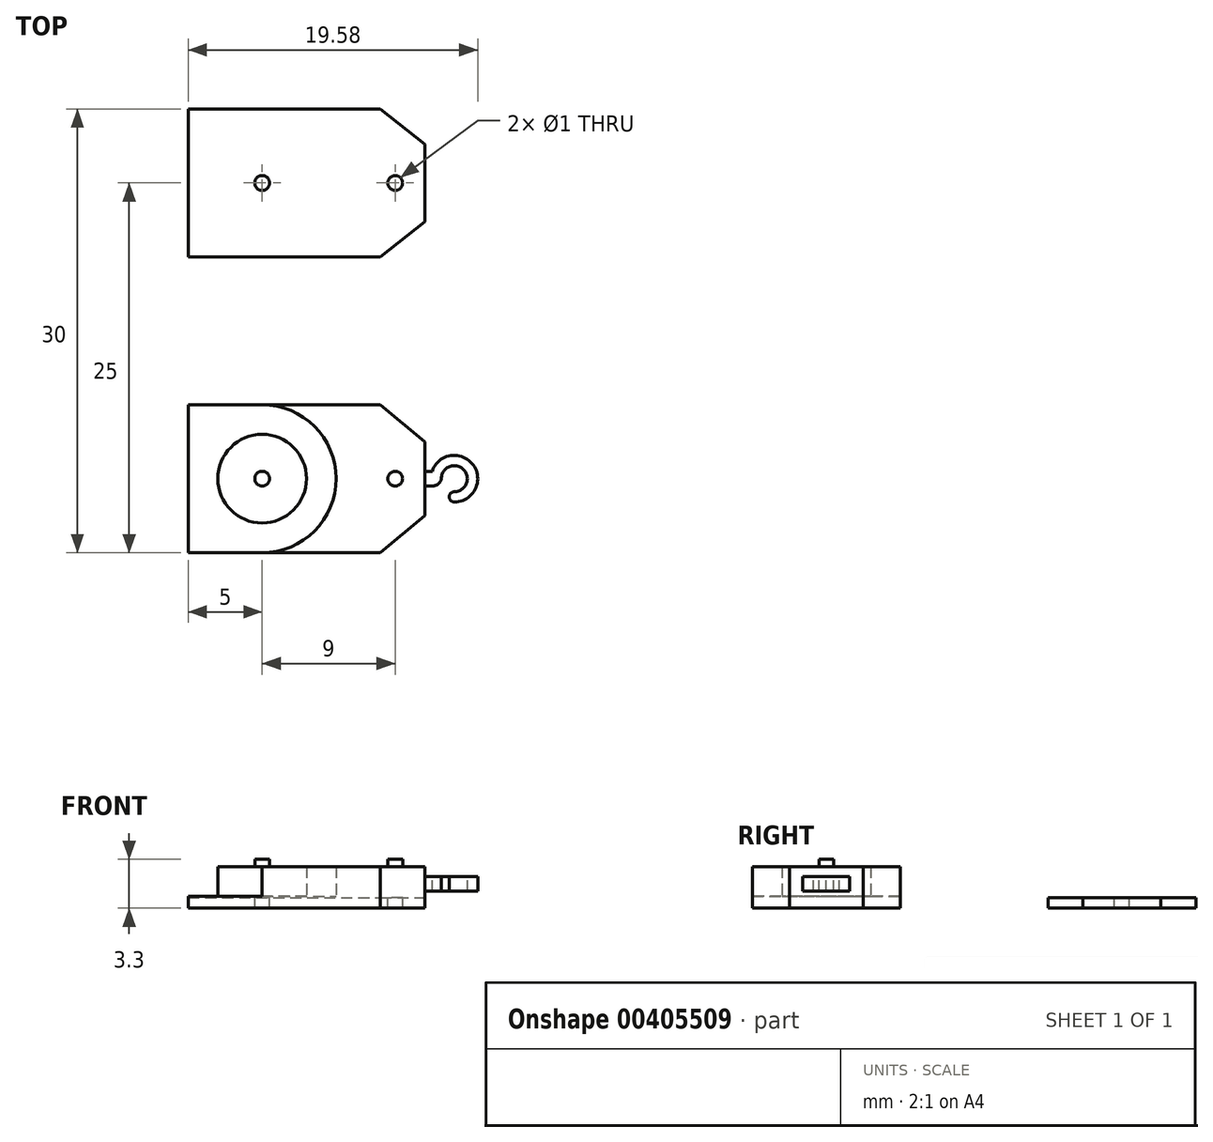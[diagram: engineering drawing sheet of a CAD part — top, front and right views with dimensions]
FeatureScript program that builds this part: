
annotation { "Feature Type Name" : "Feature", "Feature Type Description" : "" }
export const myFeature = defineFeature(function(context is Context, id is Id, definition is map)
    precondition{}
    {
        {
            var Q0;
            Q0=qCreatedBy(makeId("Top.planeOp"),FACE);
            var sketch = newSketch(context, id + "F0", { "sketchPlane" : qUnion([Q0])});
            skLineSegment(sketch, "E0", {"start": v(0, 0) * mm, "end": v(0, -10) * mm});
            skLineSegment(sketch, "E1", {"start": v(0, -10) * mm, "end": v(13, -10) * mm});
            skLineSegment(sketch, "E2", {"start": v(0, 0) * mm, "end": v(13, 0) * mm});
            skLineSegment(sketch, "E3", {"start": v(13, 0) * mm, "end": v(16, -2.5) * mm});
            skLineSegment(sketch, "E4", {"start": v(16, -2.5) * mm, "end": v(16, -7.5) * mm});
            skLineSegment(sketch, "E5", {"start": v(16, -7.5) * mm, "end": v(13, -10) * mm});
            skLineSegment(sketch, "E6", {"start": v(16, -5) * mm, "end": v(0, -5) * mm, "construction": true});
            skSolve(sketch);
        }
        {
            var Q0;
            Q0=makeQuery(id+"F0.imprint","IMPRINT",FACE,{"disambiguationData":[TD([[makeQuery(id+"F0.imprint","IMPRINT",EDGE,{"derivedFrom":sQuery(id+"F0.wireOp",EDGE,"E0")}),1.0]])]});
            extrude(context, id + "F1", {"entities" : qUnion([Q0]), "depth" : 0.8 * mm});
        }
        {
            var Q0;
            Q0=makeQuery(id+"F1.opExtrude","CAP_FACE",FACE,{"disambiguationData":[OSD([sQuery(id+"F0.wireOp",EDGE,"E0"),sQuery(id+"F0.wireOp",EDGE,"E1"),sQuery(id+"F0.wireOp",EDGE,"E2"),sQuery(id+"F0.wireOp",EDGE,"E3"),sQuery(id+"F0.wireOp",EDGE,"E4"),sQuery(id+"F0.wireOp",EDGE,"E5")])],"isStart":false});
            var sketch = newSketch(context, id + "F2", { "sketchPlane" : qUnion([Q0])});
            skLineSegment(sketch, "E7", {"start": v(0, -5) * mm, "end": v(5, -5) * mm, "construction": true});
            skCircle(sketch, "E8", {"center": v(5, -5) * mm, "radius": 3 * mm});
            skLineSegment(sketch, "E9", {"start": v(0, 0) * mm, "end": v(0, -1) * mm, "construction": true});
            skArc(sketch, "E10", {"start": v(5, 0) * mm, "mid": v(10, -5) * mm, "end": v(5, -10) * mm});
            skArc(sketch, "E11", {"start": v(5, -1) * mm, "mid": v(9, -5) * mm, "end": v(5, -9) * mm});
            skLineSegment(sketch, "E12", {"start": v(0, -1) * mm, "end": v(5, -1) * mm});
            skLineSegment(sketch, "E13", {"start": v(5, -9) * mm, "end": v(0, -9) * mm});
            skLineSegment(sketch, "E14", {"start": v(0, -9) * mm, "end": v(0, -10) * mm});
            skLineSegment(sketch, "E15", {"start": v(0, -10) * mm, "end": v(5, -10) * mm});
            skLineSegment(sketch, "E16", {"start": v(0, 0) * mm, "end": v(5, 0) * mm});
            skLineSegment(sketch, "E17", {"start": v(16, -7.5) * mm, "end": v(13, -10) * mm});
            skLineSegment(sketch, "E18", {"start": v(13, -10) * mm, "end": v(12, -10) * mm});
            skLineSegment(sketch, "E19", {"start": v(12, -10) * mm, "end": v(12, 0) * mm});
            skLineSegment(sketch, "E20", {"start": v(12, 0) * mm, "end": v(13, 0) * mm});
            skLineSegment(sketch, "E21", {"start": v(13, 0) * mm, "end": v(16, -2.5) * mm});
            skLineSegment(sketch, "E22", {"start": v(16, -2.5) * mm, "end": v(16, -7.5) * mm});
            skSolve(sketch);
        }
        {
            var Q0;
            Q0 = qSketchRegion(id + "F2", true);
            var Q1;
            Q1=makeQuery(id+"F2.imprint","IMPRINT",FACE,{"disambiguationData":[TD([[makeQuery(id+"F2.imprint","IMPRINT",EDGE,{"derivedFrom":sQuery(id+"F2.wireOp",EDGE,"E10")}),-1.0]])]});
            extrude(context, id + "F3", {"entities" : qUnion([Q0, Q1]), "operationType" : NewBodyOperationType.ADD, "depth" : 2 * mm});
        }
        {
            var Q0;
            Q0=makeQuery(id+"F3.opExtrude","CAP_FACE",FACE,{"disambiguationData":[OSD([sQuery(id+"F2.wireOp",EDGE,"E8")])],"isStart":false});
            var sketch = newSketch(context, id + "F4", { "sketchPlane" : qUnion([Q0])});
            skCircle(sketch, "E23", {"center": v(5, -5) * mm, "radius": 0.5 * mm});
            skSolve(sketch);
        }
        {
            var Q0;
            Q0 = qSketchRegion(id + "F4", true);
            extrude(context, id + "F5", {"entities" : qUnion([Q0]), "operationType" : NewBodyOperationType.ADD, "depth" : 0.5 * mm});
        }
        {
            var Q0;
            Q0=makeQuery(id+"F3.opExtrude","CAP_FACE",FACE,{"disambiguationData":[OSD([sQuery(id+"F2.wireOp",EDGE,"E17"),sQuery(id+"F2.wireOp",EDGE,"E18"),sQuery(id+"F2.wireOp",EDGE,"E19"),sQuery(id+"F2.wireOp",EDGE,"E20"),sQuery(id+"F2.wireOp",EDGE,"E21"),sQuery(id+"F2.wireOp",EDGE,"E22")])],"isStart":false});
            var sketch = newSketch(context, id + "F6", { "sketchPlane" : qUnion([Q0])});
            skLineSegment(sketch, "E24", {"start": v(16, -5) * mm, "end": v(12, -5) * mm, "construction": true});
            skCircle(sketch, "E25", {"center": v(14, -5) * mm, "radius": 0.5 * mm});
            skSolve(sketch);
        }
        {
            var Q0;
            Q0 = qSketchRegion(id + "F6", true);
            extrude(context, id + "F7", {"entities" : qUnion([Q0]), "operationType" : NewBodyOperationType.ADD, "depth" : 0.5 * mm});
        }
        {
            var Q0;
            Q0=makeQuery(id+"F3.boolean.opBoolean","MERGE",FACE,{"derivedFrom":[makeQuery(id+"F1.opExtrude","SWEPT_FACE",FACE,{"disambiguationData":[OSD([sQuery(id+"F0.wireOp",EDGE,"E4")])]}),makeQuery(id+"F3.opExtrude","SWEPT_FACE",FACE,{"disambiguationData":[OSD([sQuery(id+"F2.wireOp",EDGE,"E22")])]})]});
            var sketch = newSketch(context, id + "F8", { "sketchPlane" : qUnion([Q0])});
            skLineSegment(sketch, "E26", {"start": v(-7.5, 0) * mm, "end": v(-7.5, 0.5) * mm, "construction": true});
            skLineSegment(sketch, "E27", {"start": v(-2.5, 0.5) * mm, "end": v(-2.5, 2.8) * mm, "construction": true});
            skLineSegment(sketch, "E28", {"start": v(-7.5, 1.65) * mm, "end": v(-7.5, 1.15) * mm});
            skPoint(sketch, "E28.startSnap0", {"position": v(-2.5, 1.65) * mm});
            skLineSegment(sketch, "E29", {"start": v(-7.5, 1.15) * mm, "end": v(-2.5, 1.15) * mm});
            skLineSegment(sketch, "E30", {"start": v(-2.5, 1.15) * mm, "end": v(-2.5, 2.15) * mm});
            skLineSegment(sketch, "E31", {"start": v(-2.5, 2.15) * mm, "end": v(-7.5, 2.15) * mm});
            skLineSegment(sketch, "E32", {"start": v(-7.5, 2.15) * mm, "end": v(-7.5, 1.65) * mm});
            skSolve(sketch);
        }
        {
            var Q0;
            Q0=makeQuery(id+"F8.imprint","IMPRINT",FACE,{"disambiguationData":[TD([[makeQuery(id+"F8.imprint","IMPRINT",EDGE,{"derivedFrom":sQuery(id+"F8.wireOp",EDGE,"E28")}),1.0]])]});
            extrude(context, id + "F9", {"entities" : qUnion([Q0]), "operationType" : NewBodyOperationType.ADD, "depth" : 5 * mm});
        }
        {
            var Q0;
            Q0=makeQuery(id+"F9.opExtrude","SWEPT_FACE",FACE,{"disambiguationData":[OSD([sQuery(id+"F8.wireOp",EDGE,"E31")])]});
            var sketch = newSketch(context, id + "F10", { "sketchPlane" : qUnion([Q0])});
            skLineSegment(sketch, "E33", {"start": v(16, -5) * mm, "end": v(21, -5) * mm, "construction": true});
            skLineSegment(sketch, "E34", {"start": v(16, -5) * mm, "end": v(16, -4.5) * mm});
            skLineSegment(sketch, "E35", {"start": v(16, -4.5) * mm, "end": v(16.5, -4.5) * mm});
            skLineSegment(sketch, "E36", {"start": v(16, -5) * mm, "end": v(16, -5.5) * mm});
            skLineSegment(sketch, "E37", {"start": v(16, -5.5) * mm, "end": v(16.5, -5.5) * mm});
            skArc(sketch, "E38", {"start": v(18, -6.58) * mm, "mid": v(19.28, -4.08) * mm, "end": v(16.5, -4.5) * mm});
            skArc(sketch, "E39", {"start": v(18, -5.88) * mm, "mid": v(18.62, -4.38) * mm, "end": v(17.12, -5) * mm});
            skArc(sketch, "E40", {"start": v(16.5, -5.5) * mm, "mid": v(16.9, -5.36) * mm, "end": v(17.12, -5) * mm});
            skLineSegment(sketch, "E41", {"start": v(18, -5.88) * mm, "end": v(18, -6.58) * mm, "construction": true});
            skArc(sketch, "E42", {"start": v(18, -5.88) * mm, "mid": v(17.65, -6.23) * mm, "end": v(18, -6.58) * mm});
            skSolve(sketch);
        }
        {
            var Q0;
            {var subQ5=sQuery(id+"F10.wireOp",EDGE,"E35");Q0=makeQuery(id+"F10.imprint","IMPRINT",FACE,{"disambiguationData":[TD([[makeQuery(id+"F10.imprint","IMPRINT",EDGE,{"derivedFrom":subQ5}),1.0]])]});}
            extrude(context, id + "F11", {"entities" : qUnion([Q0]), "operationType" : NewBodyOperationType.REMOVE, "oppositeDirection" : true, "depth" : 25 * mm});
        }
        {
            var Q0;
            Q0=qCreatedBy(makeId("Top.planeOp"),FACE);
            var sketch = newSketch(context, id + "F12", { "sketchPlane" : qUnion([Q0])});
            skLineSegment(sketch, "E43", {"start": v(0, 0) * mm, "end": v(0, 10) * mm, "construction": true});
            skLineSegment(sketch, "E44", {"start": v(0, 10) * mm, "end": v(13, 10) * mm});
            skLineSegment(sketch, "E45", {"start": v(13, 10) * mm, "end": v(16, 12.37) * mm});
            skLineSegment(sketch, "E46", {"start": v(16, 12.37) * mm, "end": v(16, 17.63) * mm});
            skLineSegment(sketch, "E47", {"start": v(16, 17.63) * mm, "end": v(13, 20) * mm});
            skLineSegment(sketch, "E48", {"start": v(13, 20) * mm, "end": v(0, 20) * mm});
            skLineSegment(sketch, "E49", {"start": v(0, 20) * mm, "end": v(0, 10) * mm});
            skLineSegment(sketch, "E50", {"start": v(16, 15) * mm, "end": v(0, 15) * mm, "construction": true});
            skSolve(sketch);
        }
        {
            var Q0;
            Q0=makeQuery(id+"F12.imprint","IMPRINT",FACE,{"disambiguationData":[TD([[makeQuery(id+"F12.imprint","IMPRINT",EDGE,{"derivedFrom":sQuery(id+"F12.wireOp",EDGE,"E44")}),1.0]])]});
            extrude(context, id + "F13", {"entities" : qUnion([Q0]), "depth" : 0.7 * mm});
        }
        {
            var Q0;
            Q0=makeQuery(id+"F13.opExtrude","CAP_FACE",FACE,{"disambiguationData":[OSD([sQuery(id+"F12.wireOp",EDGE,"E44"),sQuery(id+"F12.wireOp",EDGE,"E45"),sQuery(id+"F12.wireOp",EDGE,"E46"),sQuery(id+"F12.wireOp",EDGE,"E47"),sQuery(id+"F12.wireOp",EDGE,"E48"),sQuery(id+"F12.wireOp",EDGE,"E49")])],"isStart":false});
            var sketch = newSketch(context, id + "F14", { "sketchPlane" : qUnion([Q0])});
            skLineSegment(sketch, "E51", {"start": v(0, 15) * mm, "end": v(5, 15) * mm, "construction": true});
            skCircle(sketch, "E52", {"center": v(5, 15) * mm, "radius": 0.5 * mm});
            skLineSegment(sketch, "E53", {"start": v(13, 20) * mm, "end": v(12, 20) * mm, "construction": true});
            skLineSegment(sketch, "E54", {"start": v(12, 20) * mm, "end": v(12, 10) * mm, "construction": true});
            skLineSegment(sketch, "E55", {"start": v(16, 15) * mm, "end": v(12, 15) * mm, "construction": true});
            skCircle(sketch, "E56", {"center": v(14, 15) * mm, "radius": 0.5 * mm});
            skSolve(sketch);
        }
        {
            var Q0;
            Q0 = qSketchRegion(id + "F14", true);
            extrude(context, id + "F15", {"entities" : qUnion([Q0]), "operationType" : NewBodyOperationType.REMOVE, "oppositeDirection" : true, "depth" : 25 * mm});
        }
    });
